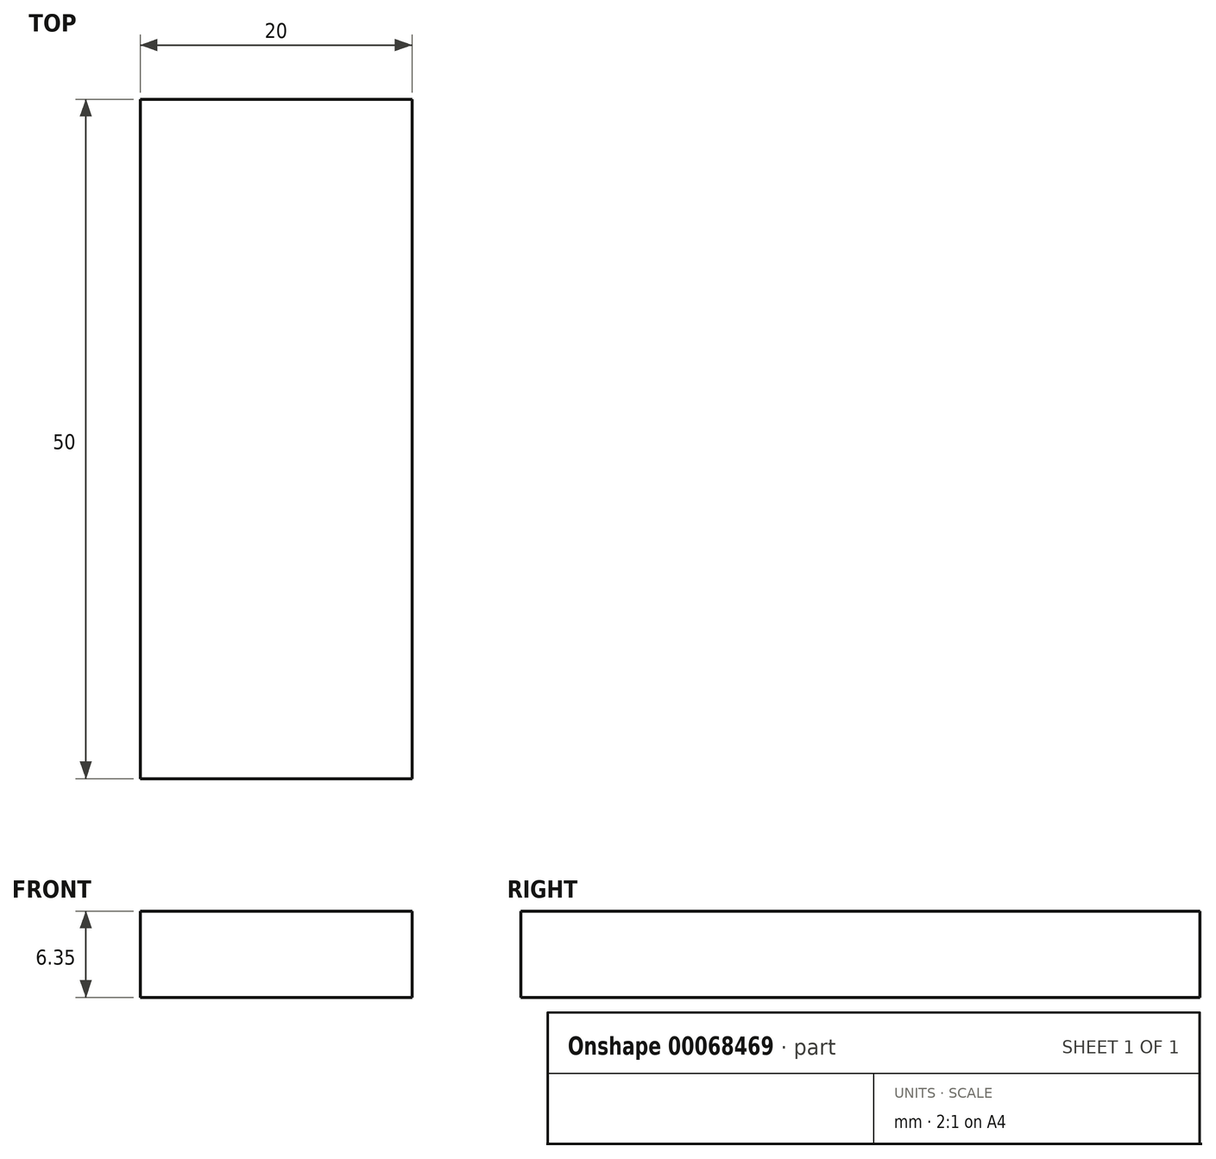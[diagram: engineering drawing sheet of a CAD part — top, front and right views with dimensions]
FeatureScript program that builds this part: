
annotation { "Feature Type Name" : "Feature", "Feature Type Description" : "" }
export const myFeature = defineFeature(function(context is Context, id is Id, definition is map)
    precondition{}
    {
        {
            var Q0;
            Q0=qCreatedBy(makeId("Top.planeOp"),FACE);
            var sketch = newSketch(context, id + "F0", { "sketchPlane" : qUnion([Q0])});
            skLineSegment(sketch, "E0.rect.bottom", {"start": v(10, 25) * mm, "end": v(-10, 25) * mm});
            skLineSegment(sketch, "E0.rect.top", {"start": v(10, -25) * mm, "end": v(-10, -25) * mm});
            skLineSegment(sketch, "E0.rect.left", {"start": v(10, 25) * mm, "end": v(10, -25) * mm});
            skLineSegment(sketch, "E0.rect.right", {"start": v(-10, 25) * mm, "end": v(-10, -25) * mm});
            skPoint(sketch, "E0.rect.middle", {"position": v(0, 0) * mm});
            skSolve(sketch);
        }
        {
            var Q0;
            Q0 = qSketchRegion(id + "F0", true);
            extrude(context, id + "F1", {"entities" : qUnion([Q0]), "depth" : 6.35 * mm});
        }
    });
